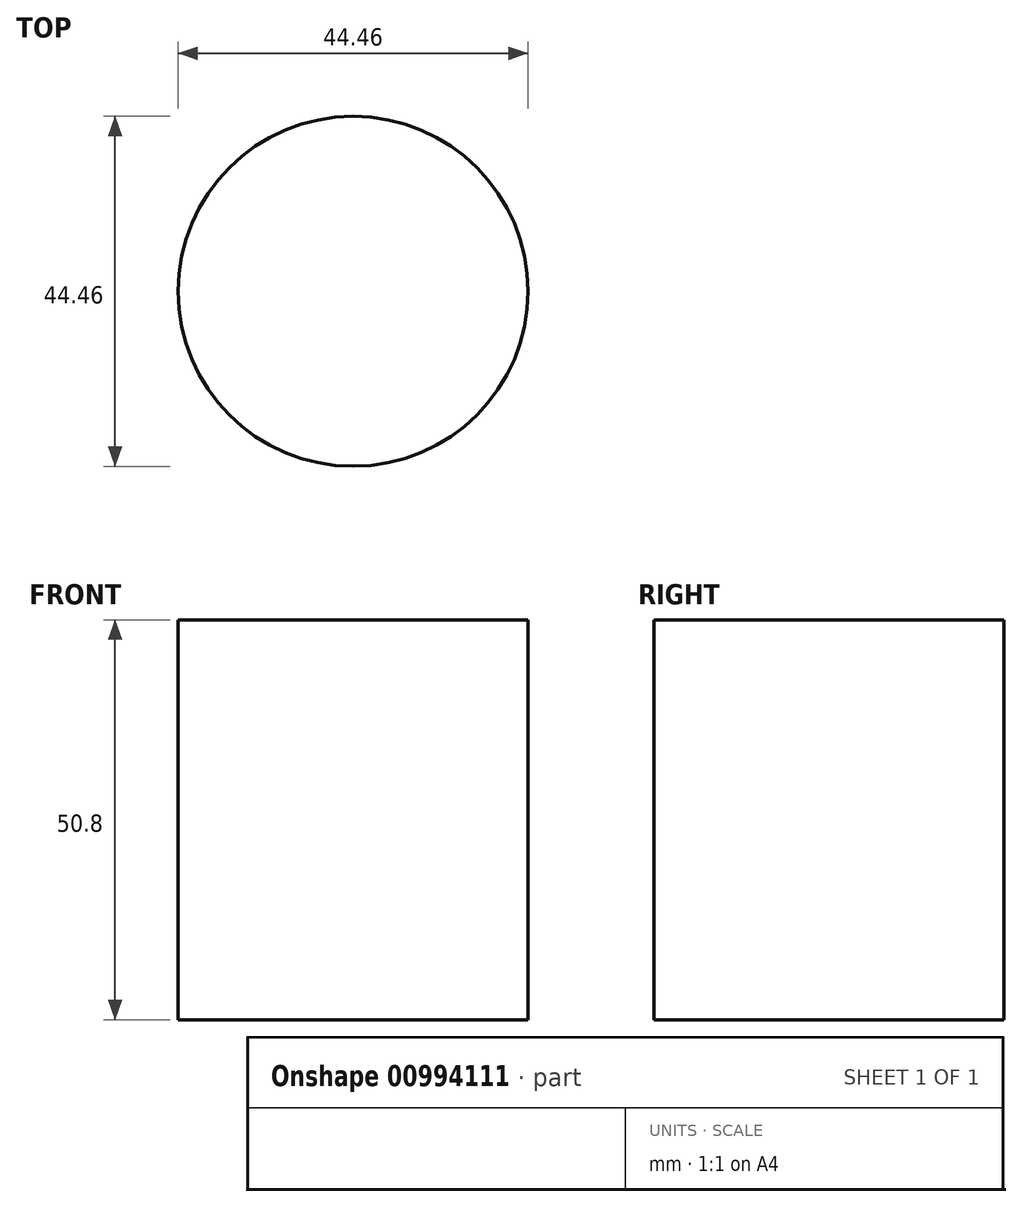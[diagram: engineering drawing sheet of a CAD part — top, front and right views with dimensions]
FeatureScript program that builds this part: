
annotation { "Feature Type Name" : "Feature", "Feature Type Description" : "" }
export const myFeature = defineFeature(function(context is Context, id is Id, definition is map)
    precondition{}
    {
        {
            var Q0;
            Q0=qCreatedBy(makeId("Top.planeOp"),FACE);
            var sketch = newSketch(context, id + "F0", { "sketchPlane" : qUnion([Q0])});
            skCircle(sketch, "E0", {"center": v(0, 0) * mm, "radius": 22.23 * mm});
            skSolve(sketch);
        }
        {
            var Q0;
            Q0 = qSketchRegion(id + "F0", true);
            extrude(context, id + "F1", {"entities" : qUnion([Q0]), "depth" : 50.8 * mm, "offsetDistance" : 25.4 * mm});
        }
    });
